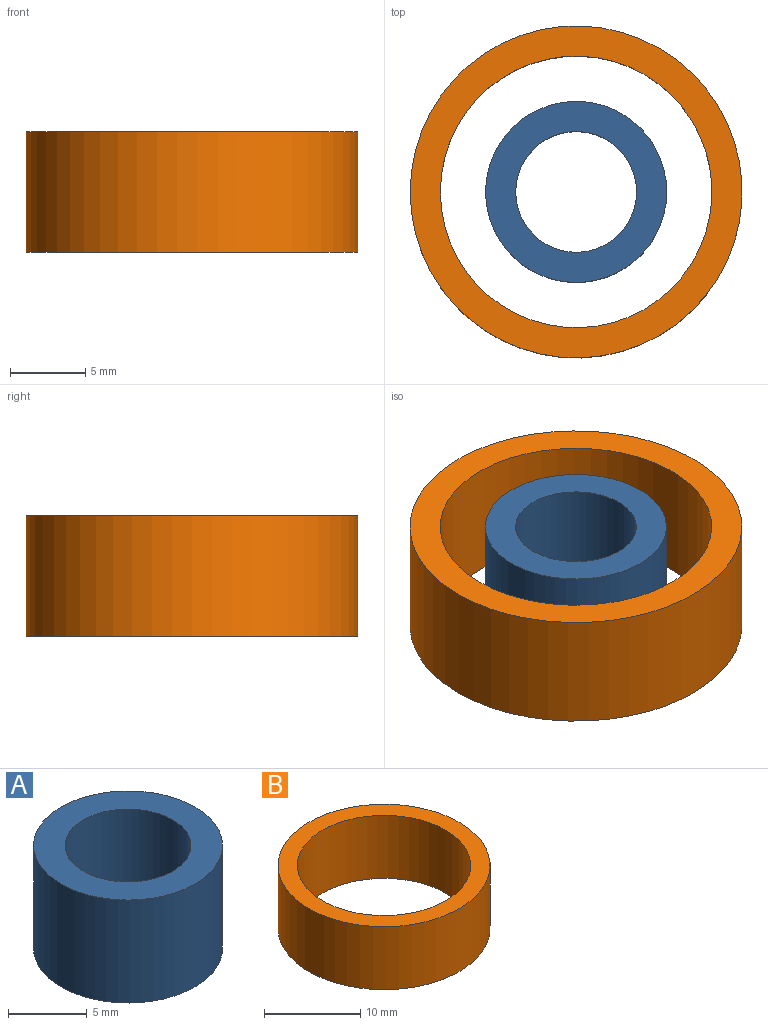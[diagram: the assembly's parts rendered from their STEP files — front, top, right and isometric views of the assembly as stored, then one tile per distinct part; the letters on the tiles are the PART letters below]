
ASSEMBLY  parts=2 mates=1
PART A: 4 faces, bbox 12x12x8 mm
  f0: cylinder r=4mm len=8mm, axis (0,0,-1), area 201.1mm2, adj f2,f3
  f1: cylinder r=6mm len=12mm, axis (0,0,-1), area 301.6mm2, adj f2,f3
  f2: plane 12x12mm, normal (0,0,1), area 62.8mm2, adj f0,f1
  f3: plane 12x12mm, normal (0,0,-1), area 62.8mm2, adj f0,f1
PART B: 4 faces, bbox 22x22x8 mm
  f0: cylinder r=9mm len=18mm, axis (0,0,-1), area 452.4mm2, adj f2,f3
  f1: cylinder r=11mm len=22mm, axis (0,0,-1), area 552.9mm2, adj f2,f3
  f2: plane 22x22mm, normal (0,0,1), area 125.7mm2, adj f0,f1
  f3: plane 22x22mm, normal (0,0,-1), area 125.7mm2, adj f0,f1
PLACE A at identity
PLACE B rot(axis=(0,0,1),180deg) t=(0,0,0)mm
MATE fastened B.f1 <-> A.f1  axis (0,0,1) through (0,0,8)mm
